# Revit family: ElectricalFixture_WiringAccessories_Hager_Sollysta_DecorativeRaisedEuroPlates
name_source: partatom
category: Electrical Fixtures
revit_build: Autodesk Revit 2015 (Build: 20160512_1515(x64)
units: mm (PartAtom-declared; Revit-internal decimal feet)

## types (12) — shared parameters
CE Approval = Yes
Default Elevation = 1219.2 mm  [stored 4 ft]
Design Country = China
Expected Life = 25 years
Extrusion From Wall = 9 mm  [stored 0.0295276 ft]
Frequency = 50/60Hz
Gross Weight kg = 0.165
LED Indicator Switch = No
Manufacturer = Hager
Manufacturer Country = United Kingdom
Manufacturer Website = http://www.hager.co.uk
Overall Depth = 26.1 mm
Overall Height = 86 mm  [stored 0.282152 ft]
Packaging Recyclable = Yes
Product Family = DecorativeEuroAccomodationPlates&Modules
Product Group = WiringAccessories
Product Literature = http://www.hager.co.uk
Product Range = Sollysta
Product URL = http://www.hager.co.uk
Reference Standard = BS 1363-2
Shape = Rectangular
Shipping Weight kg = 0.188
Supply Phase = 1
Switch = Yes
Switch Width = 100 mm  [stored 0.328084 ft]
SwitchHeight = 50 mm  [stored 0.164042 ft]
Type = ElectricalFixture
Voltage (Volts) = 230V/240V

## per-type parameters (varying)
| type | 1Gang | 2Gang | 4Gang | Colour | Description | EAN Code | Features | Finish | Material | Name | Overall Length | Overall Width | Technical Description |
| WRP1EUPSW | Yes | No | No | PolishedSteel | EuroStylePlate1ModulePolishedSteelWhiteInsert | 5015652261599 | EuroStylePlate1ModulePolishedSteelWhiteInsert | Polished | Hager_PolishedSteel | DecorativeEuroAccomodationPlates&Modules_WRP1EUPSW | 86 mm  [stored 0.282152 ft] | 86 mm  [stored 0.282152 ft] | EuroStylePlate1ModulePolishedSteelWhiteInsert |
| WRP2EUPSW | No | Yes | No | PolishedSteel | EuroStylePlate2ModulePolishedSteelWhiteInsert | 5015654743079 | EuroStylePlate2ModulePolishedSteelWhiteInsert | Polished | Hager_PolishedSteel | DecorativeEuroAccomodationPlates&Modules_WRP2EUPSW | 86 mm  [stored 0.282152 ft] | 86 mm  [stored 0.282152 ft] | EuroStylePlate2ModulePolishedSteelWhiteInsert |
| WRP2EUBSW | No | Yes | No | BrushedSteel | EuroStylePlate2ModuleBrushedSteelWhiteInsert | 5015654743116 | EuroStylePlate2ModuleBrushedSteelWhiteInsert | Brushed | Hager_BrushedSteel | DecorativeEuroAccomodationPlates&Modules_WRP2EUBSW | 86 mm  [stored 0.282152 ft] | 86 mm  [stored 0.282152 ft] | EuroStylePlate2ModuleBrushedSteelWhiteInsert |
| WRP2EUPBW | No | Yes | No | PolishedBrass | EuroStylePlate2ModulePolishedBrassWhiteInsert | 5015654743154 | EuroStylePlate2ModulePolishedBrassWhiteInsert | Polished | Hager_PolishedBrass | DecorativeEuroAccomodationPlates&Modules_WRP2EUPBW | 86 mm  [stored 0.282152 ft] | 86 mm  [stored 0.282152 ft] | EuroStylePlate2ModulePolishedBrassWhiteInsert |
| WRP2EUPSB | No | Yes | No | PolishedSteel | EuroStylePlate2ModulePolishedSteelBlackInsert | 5015654743093 | EuroStylePlate2ModulePolishedSteelBlackInsert | Polished | Hager_PolishedSteel | DecorativeEuroAccomodationPlates&Modules_WRP2EUPSB | 86 mm  [stored 0.282152 ft] | 86 mm  [stored 0.282152 ft] | EuroStylePlate2ModulePolishedSteelBlackInsert |
| WRP4EUPSW | No | Yes | Yes | PolishedSteel | EuroStylePlate4ModulePolishedSteelWhiteInsert | 5015654743215 | EuroStylePlate4ModulePolishedSteelWhiteInsert | Polished | Hager_PolishedSteel | DecorativeEuroAccomodationPlates&Modules_WRP4EUPSW | 146 mm  [stored 0.479003 ft] | 146 mm  [stored 0.479003 ft] | EuroStylePlate4ModulePolishedSteelWhiteInsert |
| WRP4EUBSW | No | Yes | Yes | BrushedSteel | EuroStylePlate4ModuleBrushedSteelWhiteInsert | 5015654743253 | EuroStylePlate4ModuleBrushedSteelWhiteInsert | Brushed | Hager_BrushedSteel | DecorativeEuroAccomodationPlates&Modules_WRP4EUBSW | 146 mm  [stored 0.479003 ft] | 146 mm  [stored 0.479003 ft] | EuroStylePlate4ModuleBrushedSteelWhiteInsert |
| WRP4EUPBW | No | Yes | Yes | PolishedBrass | EuroStylePlate4ModulePolishedBrassWhiteInsert | 5015654743291 | EuroStylePlate4ModulePolishedBrassWhiteInsert | Polished | Hager_PolishedBrass | DecorativeEuroAccomodationPlates&Modules_WRP4EUPBW | 146 mm  [stored 0.479003 ft] | 146 mm  [stored 0.479003 ft] | EuroStylePlate4ModulePolishedBrassWhiteInsert |
| WRP4EUPSB | No | Yes | Yes | PolishedSteel | EuroStylePlate4ModulePolishedSteelBlackInsert | 5015654743239 | EuroStylePlate4ModulePolishedSteelBlackInsert | Polished | Hager_PolishedSteel | DecorativeEuroAccomodationPlates&Modules_WRP4EUPSB | 146 mm  [stored 0.479003 ft] | 146 mm  [stored 0.479003 ft] | EuroStylePlate4ModulePolishedSteelBlackInsert |
| WRP4EUBSB | No | Yes | Yes | BrushedSteel | EuroStylePlate4ModuleBrushedSteelBlackInsert | 5015654743277 | EuroStylePlate4ModuleBrushedSteelBlackInsert | Brushed | Hager_BrushedSteel | DecorativeEuroAccomodationPlates&Modules_WRP4EUBSB | 146 mm  [stored 0.479003 ft] | 146 mm  [stored 0.479003 ft] | EuroStylePlate4ModuleBrushedSteelBlackInsert |
| WRP4EUPBB | No | Yes | Yes | PolishedBrass | EuroStylePlate4ModulePolishedBrassBlackInsert | 5015654743314 | EuroStylePlate4ModulePolishedBrassBlackInsert | Polished | Hager_PolishedBrass | DecorativeEuroAccomodationPlates&Modules_WRP4EUPBB | 146 mm  [stored 0.479003 ft] | 146 mm  [stored 0.479003 ft] | EuroStylePlate4ModulePolishedBrassBlackInsert |
| WRP4EUBNB | No | Yes | Yes | BlackNickel | EuroStylePlate4ModuleBlackNickelBlackInsert | 5015654743338 | EuroStylePlate4ModuleBlackNickelBlackInsert | Polished | Hager_BlackNickel | DecorativeEuroAccomodationPlates&Modules_WRP4EUBNB | 146 mm  [stored 0.479003 ft] | 146 mm  [stored 0.479003 ft] | EuroStylePlate4ModuleBlackNickelBlackInsert |

note: column(s) folded — value = type name in every type: Product Model Number, Unique Reference

note: [stored X ft] marks values corroborated as IEEE doubles in the binary element streams (Revit-internal decimal feet)

## geometry (parser evidence)
native form markers: Blend x4, Sweep x21
no freeform markers — native parametric forms only
